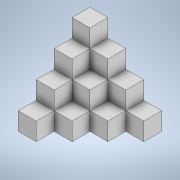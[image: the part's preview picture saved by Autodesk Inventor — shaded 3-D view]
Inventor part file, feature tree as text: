
AUTODESK INVENTOR PART (.ipt)
format: ipt  version: 2020 (Build 240168000, 168)  size: 171,008 bytes
history: native  units: mm
features: sketch x3, extrude x2, shell x1
ambient origin geometry x8: Origin, YZ Plane, XZ Plane, XY Plane, X Axis, Y Axis, Z Axis, Center Point
bodies: Solid1 (feature_tree)
feature tree (6):
  extrude  "Extrusion1"  Depth=20.0mm TaperAngle=0.0deg
  extrude  "Extrusion2"  Depth=20.0mm
  shell  "Shell1"  Thickness=20.0mm
  sketch  "Sketch1"  dims[d10=20.0mm d11=0.0mm d12=20.0mm d13=0.0mm]
  sketch  "Sketch2"  dims[d18=4.0mm d19=20.0mm d20=20.0mm]
  sketch  "Sketch4"  dims[d21=20.0mm d22=20.0mm d23=20.0mm d24=20.0mm d25=20.0mm d26=20.0mm d27=20.0mm d31=20.0mm d32=0.0mm d33=20.0mm d34=0.0mm]
